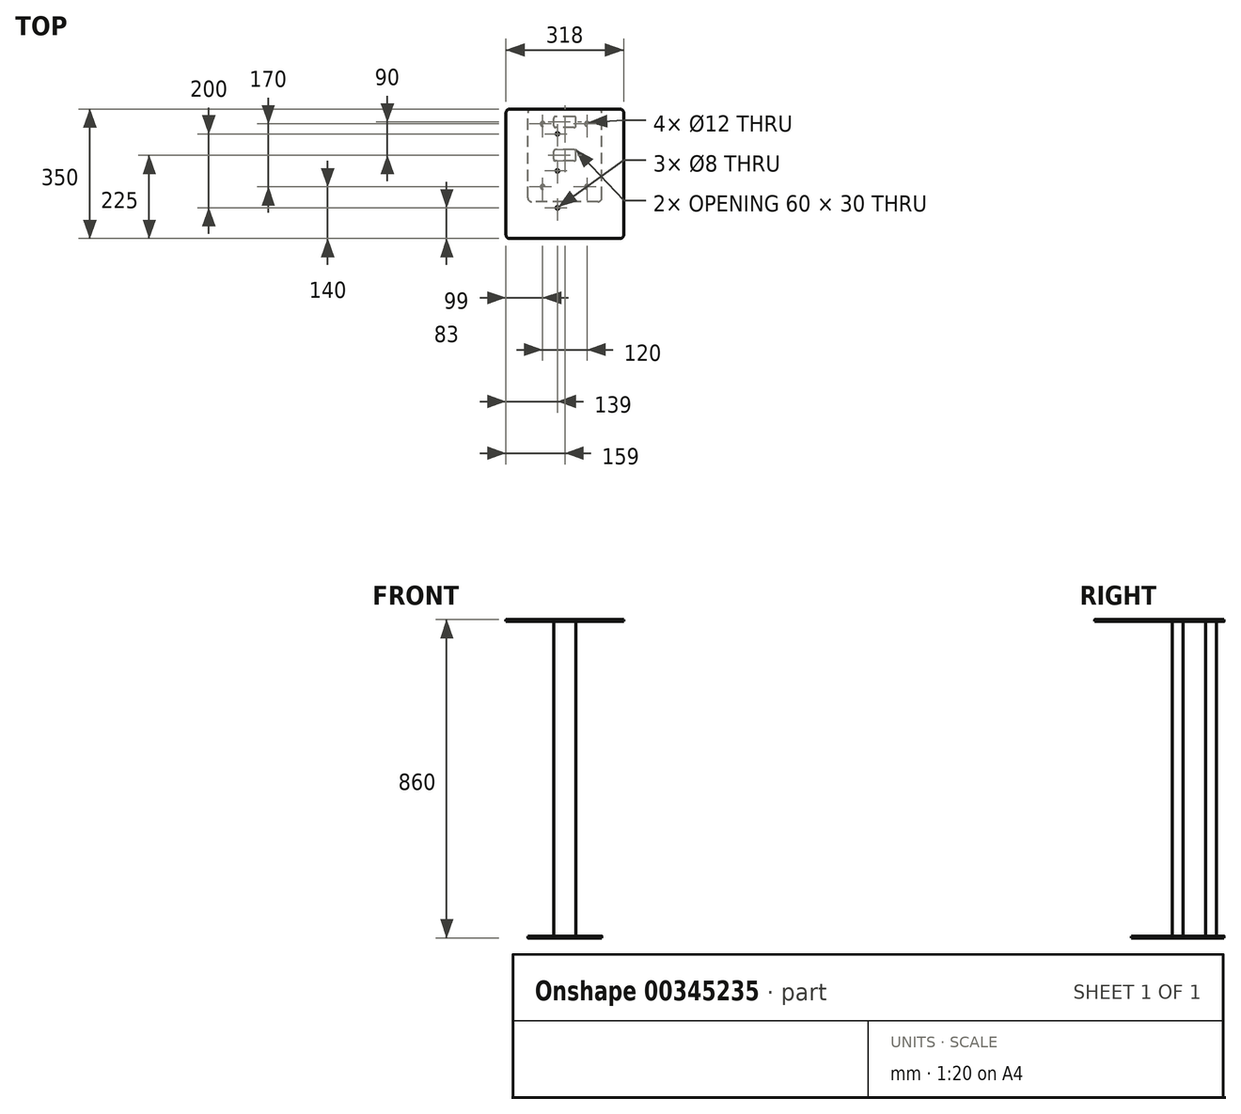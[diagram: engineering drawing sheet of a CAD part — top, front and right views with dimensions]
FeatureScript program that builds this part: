
annotation { "Feature Type Name" : "Feature", "Feature Type Description" : "" }
export const myFeature = defineFeature(function(context is Context, id is Id, definition is map)
    precondition{}
    {
        {
            var Q0;
            Q0=qCreatedBy(makeId("Top.planeOp"),FACE);
            var sketch = newSketch(context, id + "F0", { "sketchPlane" : qUnion([Q0])});
            skLineSegment(sketch, "E0.bottom", {"start": v(-159, -175) * mm, "end": v(159, -175) * mm});
            skLineSegment(sketch, "E0.top", {"start": v(-159, 175) * mm, "end": v(159, 175) * mm});
            skLineSegment(sketch, "E0.left", {"start": v(-159, -175) * mm, "end": v(-159, 175) * mm});
            skLineSegment(sketch, "E0.right", {"start": v(159, -175) * mm, "end": v(159, 175) * mm});
            skPoint(sketch, "E0.middle", {"position": v(0, 0) * mm});
            skSolve(sketch);
        }
        {
            var Q0;
            Q0 = qSketchRegion(id + "F0", true);
            extrude(context, id + "F1", {"entities" : qUnion([Q0]), "depth" : 5 * mm});
        }
        {
            var Q0;
            Q0=makeQuery(id+"F1.opExtrude","SWEPT_EDGE",EDGE,{"disambiguationData":[OSD([sQuery(id+"F0.wireOp",EDGE,"E0.bottom"),sQuery(id+"F0.wireOp",EDGE,"E0.left")])]});
            var Q1;
            Q1=makeQuery(id+"F1.opExtrude","SWEPT_EDGE",EDGE,{"disambiguationData":[OSD([sQuery(id+"F0.wireOp",EDGE,"E0.bottom"),sQuery(id+"F0.wireOp",EDGE,"E0.right")])]});
            var Q2;
            Q2=makeQuery(id+"F1.opExtrude","SWEPT_EDGE",EDGE,{"disambiguationData":[OSD([sQuery(id+"F0.wireOp",EDGE,"E0.top"),sQuery(id+"F0.wireOp",EDGE,"E0.right")])]});
            var Q3;
            Q3=makeQuery(id+"F1.opExtrude","SWEPT_EDGE",EDGE,{"disambiguationData":[OSD([sQuery(id+"F0.wireOp",EDGE,"E0.top"),sQuery(id+"F0.wireOp",EDGE,"E0.left")])]});
            fillet(context, id + "F2", {"entities" : qUnion([Q0, Q1, Q2, Q3]), "radius" : 10 * mm, "tangentPropagation" : true, "allowEdgeOverflow" : false});
        }
        {
            var Q0;
            Q0=makeQuery(id+"F1.opExtrude","CAP_FACE",FACE,{"disambiguationData":[OSD([sQuery(id+"F0.wireOp",EDGE,"E0.bottom"),sQuery(id+"F0.wireOp",EDGE,"E0.top"),sQuery(id+"F0.wireOp",EDGE,"E0.left"),sQuery(id+"F0.wireOp",EDGE,"E0.right")])],"isStart":false});
            var sketch = newSketch(context, id + "F3", { "sketchPlane" : qUnion([Q0])});
            skCircle(sketch, "E1", {"center": v(-20, -92) * mm, "radius": 4 * mm});
            skCircle(sketch, "E2", {"center": v(-20, 8) * mm, "radius": 4 * mm});
            skCircle(sketch, "E3", {"center": v(-20, 108) * mm, "radius": 4 * mm});
            skSolve(sketch);
        }
        {
            var Q0;
            Q0=sQuery(id+"F3.wireOp",VERTEX,"E1.center");
            var Q1;
            Q1=sQuery(id+"F3.wireOp",VERTEX,"E2.center");
            var Q2;
            Q2=sQuery(id+"F3.wireOp",VERTEX,"E3.center");
            var Q3;
            Q3=makeQuery(id+"F1.opExtrude","SWEPT_BODY",BODY,{"disambiguationData":[OSD([sQuery(id+"F0.wireOp",EDGE,"E0.bottom"),sQuery(id+"F0.wireOp",EDGE,"E0.top"),sQuery(id+"F0.wireOp",EDGE,"E0.left"),sQuery(id+"F0.wireOp",EDGE,"E0.right")])]});
            hole(context, id + "F4", {"style" : HoleStyle.SIMPLE, "endStyle" : HoleEndStyle.THROUGH, "holeDiameter" : 8 * mm, "isTappedThrough" : true, "tappedDepth" : 12 * mm, "tapClearance" : 3, "locations" : qUnion([Q0, Q1, Q2]), "scope" : qUnion([Q3])});
        }
        {
            var Q0;
            Q0=makeQuery(id+"F1.opExtrude","CAP_FACE",FACE,{"disambiguationData":[OSD([sQuery(id+"F0.wireOp",EDGE,"E0.bottom"),sQuery(id+"F0.wireOp",EDGE,"E0.top"),sQuery(id+"F0.wireOp",EDGE,"E0.left"),sQuery(id+"F0.wireOp",EDGE,"E0.right")])],"isStart":true});
            var sketch = newSketch(context, id + "F5", { "sketchPlane" : qUnion([Q0])});
            skLineSegment(sketch, "E4.bottom", {"start": v(30, -35) * mm, "end": v(-30, -35) * mm});
            skLineSegment(sketch, "E4.top", {"start": v(30, -65) * mm, "end": v(-30, -65) * mm});
            skLineSegment(sketch, "E4.left", {"start": v(30, -35) * mm, "end": v(30, -65) * mm});
            skLineSegment(sketch, "E4.right", {"start": v(-30, -35) * mm, "end": v(-30, -65) * mm});
            skLineSegment(sketch, "E5.bottom", {"start": v(30, -125) * mm, "end": v(-30, -125) * mm});
            skLineSegment(sketch, "E5.top", {"start": v(30, -155) * mm, "end": v(-30, -155) * mm});
            skLineSegment(sketch, "E5.left", {"start": v(30, -125) * mm, "end": v(30, -155) * mm});
            skLineSegment(sketch, "E5.right", {"start": v(-30, -125) * mm, "end": v(-30, -155) * mm});
            skSolve(sketch);
        }
        {
            var Q0;
            Q0=makeQuery(id+"F5.imprint","IMPRINT",FACE,{"disambiguationData":[TD([[makeQuery(id+"F5.imprint","IMPRINT",EDGE,{"derivedFrom":sQuery(id+"F5.wireOp",EDGE,"E4.bottom")}),1.0]])]});
            var Q1;
            Q1=makeQuery(id+"F5.imprint","IMPRINT",FACE,{"disambiguationData":[TD([[makeQuery(id+"F5.imprint","IMPRINT",EDGE,{"derivedFrom":sQuery(id+"F5.wireOp",EDGE,"E5.bottom")}),1.0]])]});
            extrude(context, id + "F6", {"entities" : qUnion([Q0, Q1]), "operationType" : NewBodyOperationType.ADD, "depth" : 850 * mm});
        }
        {
            var Q0;
            Q0=makeQuery(id+"F6.opExtrude","SWEPT_EDGE",EDGE,{"disambiguationData":[OSD([sQuery(id+"F5.wireOp",EDGE,"E5.bottom"),sQuery(id+"F5.wireOp",EDGE,"E5.right")])]});
            var Q1;
            Q1=makeQuery(id+"F6.opExtrude","SWEPT_EDGE",EDGE,{"disambiguationData":[OSD([sQuery(id+"F5.wireOp",EDGE,"E5.top"),sQuery(id+"F5.wireOp",EDGE,"E5.right")])]});
            var Q2;
            Q2=makeQuery(id+"F6.opExtrude","SWEPT_EDGE",EDGE,{"disambiguationData":[OSD([sQuery(id+"F5.wireOp",EDGE,"E5.bottom"),sQuery(id+"F5.wireOp",EDGE,"E5.left")])]});
            var Q3;
            Q3=makeQuery(id+"F6.opExtrude","SWEPT_EDGE",EDGE,{"disambiguationData":[OSD([sQuery(id+"F5.wireOp",EDGE,"E4.top"),sQuery(id+"F5.wireOp",EDGE,"E4.right")])]});
            var Q4;
            Q4=makeQuery(id+"F6.opExtrude","SWEPT_EDGE",EDGE,{"disambiguationData":[OSD([sQuery(id+"F5.wireOp",EDGE,"E4.bottom"),sQuery(id+"F5.wireOp",EDGE,"E4.right")])]});
            var Q5;
            Q5=makeQuery(id+"F6.opExtrude","SWEPT_EDGE",EDGE,{"disambiguationData":[OSD([sQuery(id+"F5.wireOp",EDGE,"E4.bottom"),sQuery(id+"F5.wireOp",EDGE,"E4.left")])]});
            var Q6;
            Q6=makeQuery(id+"F6.opExtrude","SWEPT_EDGE",EDGE,{"disambiguationData":[OSD([sQuery(id+"F5.wireOp",EDGE,"E4.top"),sQuery(id+"F5.wireOp",EDGE,"E4.left")])]});
            var Q7;
            Q7=makeQuery(id+"F6.opExtrude","SWEPT_EDGE",EDGE,{"disambiguationData":[OSD([sQuery(id+"F5.wireOp",EDGE,"E5.top"),sQuery(id+"F5.wireOp",EDGE,"E5.left")])]});
            fillet(context, id + "F7", {"entities" : qUnion([Q0, Q1, Q2, Q3, Q4, Q5, Q6, Q7]), "radius" : 5 * mm, "tangentPropagation" : true, "allowEdgeOverflow" : false});
        }
        {
            var Q0;
            Q0=makeQuery(id+"F6.opExtrude","CAP_FACE",FACE,{"disambiguationData":[OSD([sQuery(id+"F5.wireOp",EDGE,"E4.bottom"),sQuery(id+"F5.wireOp",EDGE,"E4.top"),sQuery(id+"F5.wireOp",EDGE,"E4.left"),sQuery(id+"F5.wireOp",EDGE,"E4.right")])],"isStart":false});
            var sketch = newSketch(context, id + "F8", { "sketchPlane" : qUnion([Q0])});
            skLineSegment(sketch, "E6.bottom", {"start": v(90, 75) * mm, "end": v(-90, 75) * mm});
            skLineSegment(sketch, "E6.top", {"start": v(90, -175) * mm, "end": v(-90, -175) * mm});
            skLineSegment(sketch, "E6.left", {"start": v(100, 65) * mm, "end": v(100, -165) * mm});
            skLineSegment(sketch, "E6.right", {"start": v(-100, 65) * mm, "end": v(-100, -165) * mm});
            skCircle(sketch, "E7", {"center": v(60, 35) * mm, "radius": 6 * mm});
            skCircle(sketch, "E8.MirrorC", {"center": v(-60, 35) * mm, "radius": 6 * mm});
            skPoint(sketch, "E9.visualSharp", {"position": v(-100, 75) * mm});
            skArc(sketch, "E9.filletArc", {"start": v(-90, 75) * mm, "mid": v(-97.07, 72.07) * mm, "end": v(-100, 65) * mm});
            skPoint(sketch, "E10.visualSharp", {"position": v(100, 75) * mm});
            skArc(sketch, "E10.filletArc", {"start": v(100, 65) * mm, "mid": v(97.07, 72.07) * mm, "end": v(90, 75) * mm});
            skPoint(sketch, "E11.visualSharp", {"position": v(100, -175) * mm});
            skArc(sketch, "E11.filletArc", {"start": v(90, -175) * mm, "mid": v(97.07, -172.07) * mm, "end": v(100, -165) * mm});
            skPoint(sketch, "E12.visualSharp", {"position": v(-100, -175) * mm});
            skArc(sketch, "E12.filletArc", {"start": v(-100, -165) * mm, "mid": v(-97.07, -172.07) * mm, "end": v(-90, -175) * mm});
            skCircle(sketch, "E13", {"center": v(60, -135) * mm, "radius": 6 * mm});
            skCircle(sketch, "E14", {"center": v(-60, -135) * mm, "radius": 6 * mm});
            skSolve(sketch);
        }
        {
            var Q0;
            Q0=makeQuery(id+"F8.imprint","IMPRINT",FACE,{"disambiguationData":[TD([[makeQuery(id+"F8.imprint","IMPRINT",EDGE,{"derivedFrom":sQuery(id+"F8.wireOp",EDGE,"E6.bottom")}),1.0]])]});
            var Q1;
            {var subQ3=sQuery(id+"F5.wireOp",EDGE,"E4.bottom");Q1=makeQuery(id+"F8.imprint","IMPRINT",FACE,{"disambiguationData":[TD([[makeQuery(id+"F8.imprint","IMPRINT",EDGE,{"derivedFrom":makeQuery(id+"F6.opExtrude","CAP_EDGE",EDGE,{"disambiguationData":[OSD([subQ3])],"isStart":false})}),1.0]])]});}
            extrude(context, id + "F9", {"entities" : qUnion([Q0, Q1]), "operationType" : NewBodyOperationType.ADD, "depth" : 5 * mm});
        }
    });
